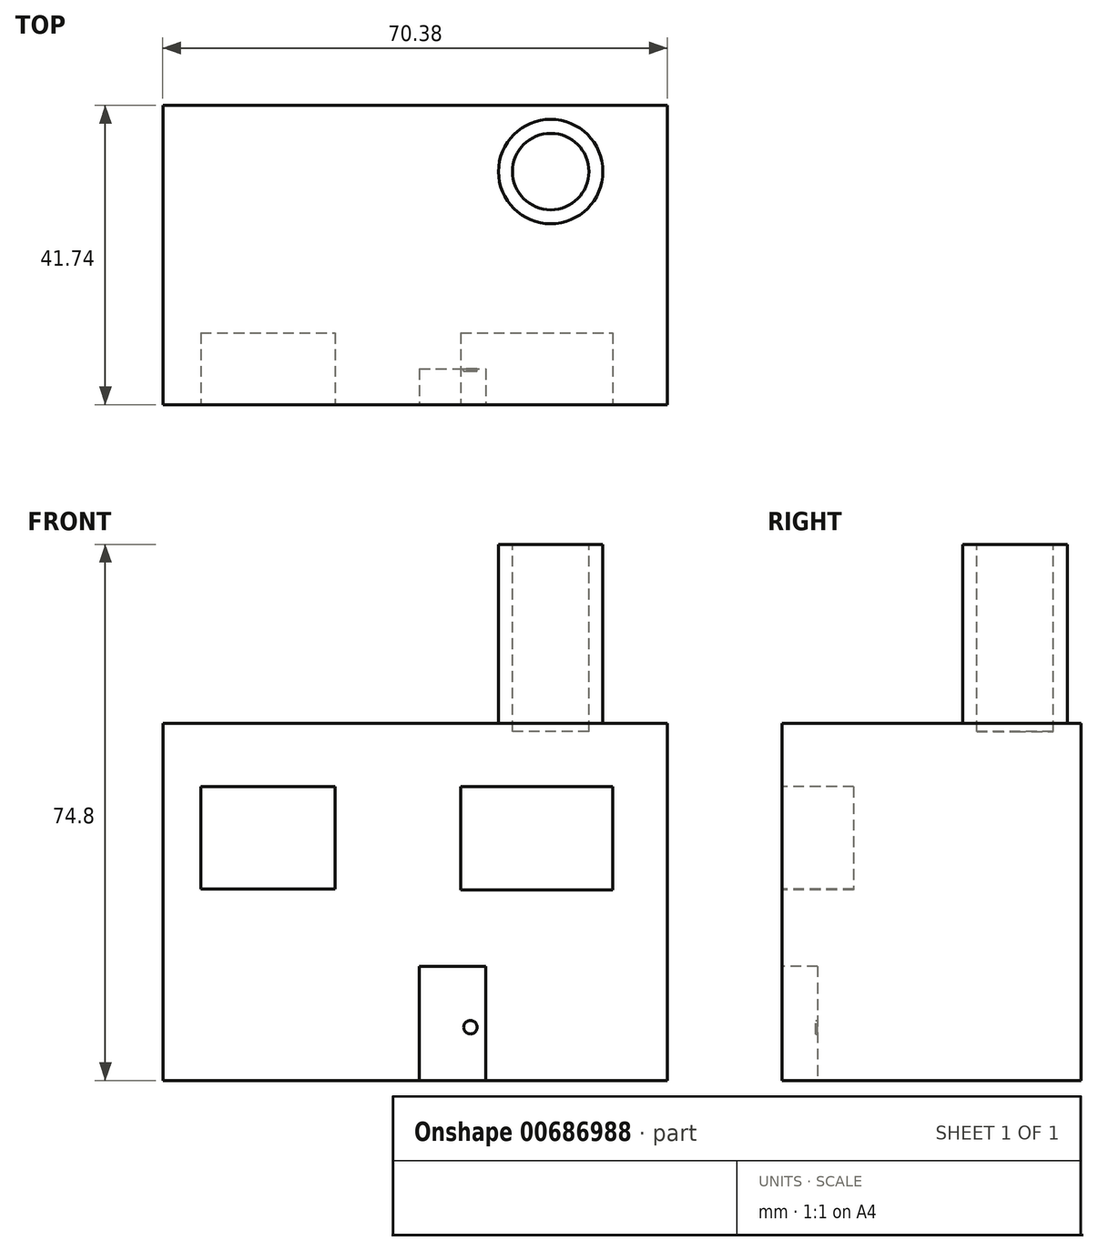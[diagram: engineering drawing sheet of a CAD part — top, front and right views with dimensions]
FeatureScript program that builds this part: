
annotation { "Feature Type Name" : "Feature", "Feature Type Description" : "" }
export const myFeature = defineFeature(function(context is Context, id is Id, definition is map)
    precondition{}
    {
        {
            var Q0;
            Q0=qCreatedBy(makeId("Top.planeOp"),FACE);
            var sketch = newSketch(context, id + "F0", { "sketchPlane" : qUnion([Q0])});
            skLineSegment(sketch, "E0.bottom", {"start": v(-35.8, 22.33) * mm, "end": v(34.58, 22.33) * mm});
            skLineSegment(sketch, "E0.top", {"start": v(-35.8, -19.41) * mm, "end": v(34.58, -19.41) * mm});
            skLineSegment(sketch, "E0.left", {"start": v(-35.8, 22.33) * mm, "end": v(-35.8, -19.41) * mm});
            skLineSegment(sketch, "E0.right", {"start": v(34.58, 22.33) * mm, "end": v(34.58, -19.41) * mm});
            skSolve(sketch);
        }
        {
            var Q0;
            Q0 = qSketchRegion(id + "F0", true);
            extrude(context, id + "F1", {"entities" : qUnion([Q0]), "depth" : 49.8 * mm, "offsetDistance" : 25 * mm});
        }
        {
            var Q0;
            Q0=makeQuery(id+"F1.opExtrude","SWEPT_FACE",FACE,{"disambiguationData":[OSD([sQuery(id+"F0.wireOp",EDGE,"E0.top")])]});
            var sketch = newSketch(context, id + "F2", { "sketchPlane" : qUnion([Q0])});
            skLineSegment(sketch, "E1.bottom", {"start": v(0, 15.93) * mm, "end": v(9.25, 15.93) * mm});
            skLineSegment(sketch, "E1.top", {"start": v(0, 0) * mm, "end": v(9.25, 0) * mm});
            skLineSegment(sketch, "E1.left", {"start": v(0, 15.93) * mm, "end": v(0, 0) * mm});
            skLineSegment(sketch, "E1.right", {"start": v(9.25, 15.93) * mm, "end": v(9.25, 0) * mm});
            skSolve(sketch);
        }
        {
            var Q0;
            Q0 = qSketchRegion(id + "F2", true);
            extrude(context, id + "F3", {"entities" : qUnion([Q0]), "operationType" : NewBodyOperationType.REMOVE, "oppositeDirection" : true, "depth" : 5 * mm, "offsetDistance" : 25 * mm});
        }
        {
            var Q0;
            Q0=makeQuery(id+"F1.opExtrude","SWEPT_FACE",FACE,{"disambiguationData":[OSD([sQuery(id+"F0.wireOp",EDGE,"E0.top")])]});
            var sketch = newSketch(context, id + "F4", { "sketchPlane" : qUnion([Q0])});
            skLineSegment(sketch, "E2.bottom", {"start": v(-30.52, 40.98) * mm, "end": v(-11.77, 40.98) * mm});
            skLineSegment(sketch, "E2.top", {"start": v(-30.52, 26.72) * mm, "end": v(-11.77, 26.72) * mm});
            skLineSegment(sketch, "E2.left", {"start": v(-30.52, 40.98) * mm, "end": v(-30.52, 26.72) * mm});
            skLineSegment(sketch, "E2.right", {"start": v(-11.77, 40.98) * mm, "end": v(-11.77, 26.72) * mm});
            skLineSegment(sketch, "E3.bottom", {"start": v(5.78, 40.98) * mm, "end": v(26.99, 40.98) * mm});
            skLineSegment(sketch, "E3.top", {"start": v(5.78, 26.6) * mm, "end": v(26.99, 26.6) * mm});
            skLineSegment(sketch, "E3.left", {"start": v(5.78, 40.98) * mm, "end": v(5.78, 26.6) * mm});
            skLineSegment(sketch, "E3.right", {"start": v(26.99, 40.98) * mm, "end": v(26.99, 26.6) * mm});
            skSolve(sketch);
        }
        {
            var Q0;
            Q0 = qSketchRegion(id + "F4", true);
            extrude(context, id + "F5", {"entities" : qUnion([Q0]), "operationType" : NewBodyOperationType.REMOVE, "oppositeDirection" : true, "depth" : 10 * mm, "offsetDistance" : 25 * mm});
        }
        {
            var Q0;
            Q0=makeQuery(id+"F1.opExtrude","CAP_FACE",FACE,{"disambiguationData":[OSD([sQuery(id+"F0.wireOp",EDGE,"E0.bottom"),sQuery(id+"F0.wireOp",EDGE,"E0.top"),sQuery(id+"F0.wireOp",EDGE,"E0.left"),sQuery(id+"F0.wireOp",EDGE,"E0.right")])],"isStart":false});
            var sketch = newSketch(context, id + "F6", { "sketchPlane" : qUnion([Q0])});
            skCircle(sketch, "E4", {"center": v(18.32, 13.1) * mm, "radius": 7.28 * mm});
            skSolve(sketch);
        }
        {
            var Q0;
            Q0 = qSketchRegion(id + "F6", true);
            extrude(context, id + "F7", {"entities" : qUnion([Q0]), "operationType" : NewBodyOperationType.ADD, "depth" : 25 * mm, "offsetDistance" : 25 * mm});
        }
        {
            var Q0;
            Q0=makeQuery(id+"F7.opExtrude","CAP_FACE",FACE,{"disambiguationData":[OSD([sQuery(id+"F6.wireOp",EDGE,"E4")])],"isStart":false});
            var sketch = newSketch(context, id + "F8", { "sketchPlane" : qUnion([Q0])});
            skCircle(sketch, "E5", {"center": v(18.32, 13.1) * mm, "radius": 5.34 * mm});
            skSolve(sketch);
        }
        {
            var Q0;
            Q0 = qSketchRegion(id + "F8", true);
            extrude(context, id + "F9", {"entities" : qUnion([Q0]), "operationType" : NewBodyOperationType.REMOVE, "oppositeDirection" : true, "depth" : 26.1 * mm, "offsetDistance" : 25 * mm});
        }
        {
            var Q0;
            Q0=makeQuery(id+"F3.boolean.opBoolean","COPY",FACE,{"derivedFrom":makeQuery(id+"F3.opExtrude","CAP_FACE",FACE,{"disambiguationData":[OSD([sQuery(id+"F2.wireOp",EDGE,"E1.bottom"),sQuery(id+"F2.wireOp",EDGE,"E1.top"),sQuery(id+"F2.wireOp",EDGE,"E1.left"),sQuery(id+"F2.wireOp",EDGE,"E1.right")])],"isStart":false})});
            var sketch = newSketch(context, id + "F10", { "sketchPlane" : qUnion([Q0])});
            skCircle(sketch, "E6", {"center": v(7.12, 7.42) * mm, "radius": 0.94 * mm});
            skSolve(sketch);
        }
        {
            var Q0;
            Q0 = qSketchRegion(id + "F10", true);
            extrude(context, id + "F11", {"entities" : qUnion([Q0]), "operationType" : NewBodyOperationType.ADD, "depth" : 0.3 * mm, "offsetDistance" : 25 * mm});
        }
    });
